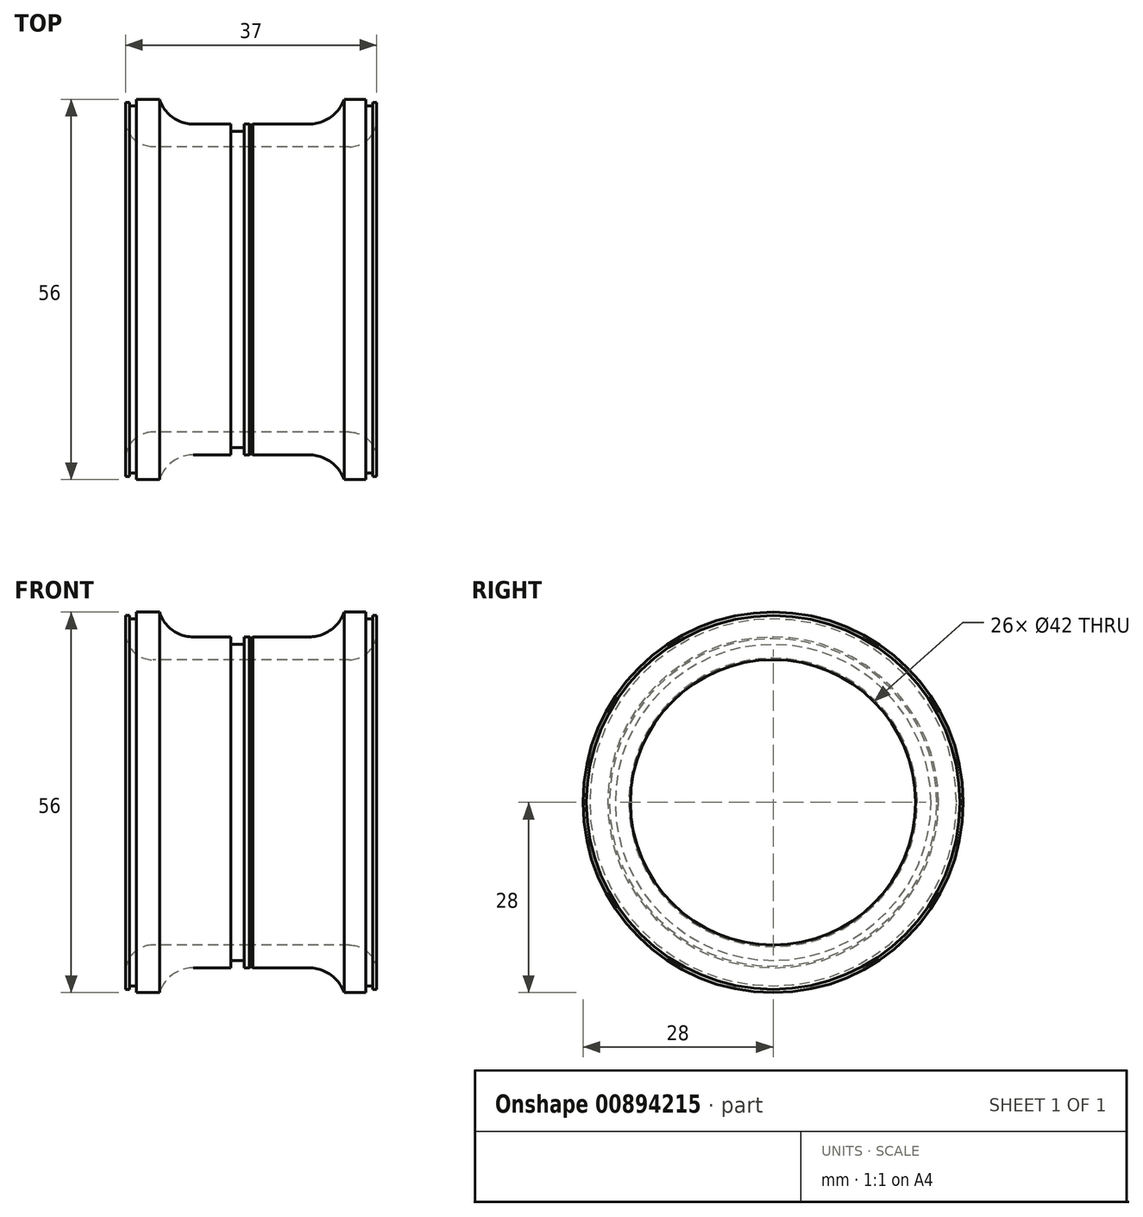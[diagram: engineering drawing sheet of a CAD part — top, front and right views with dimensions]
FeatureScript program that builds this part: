
annotation { "Feature Type Name" : "Feature", "Feature Type Description" : "" }
export const myFeature = defineFeature(function(context is Context, id is Id, definition is map)
    precondition{}
    {
        {
            var Q0;
            Q0=qCreatedBy(makeId("Front.planeOp"),FACE);
            var sketch = newSketch(context, id + "F0", { "sketchPlane" : qUnion([Q0])});
            skLineSegment(sketch, "E0", {"start": v(18.25, 21) * mm, "end": v(18.5, 21.25) * mm});
            skLineSegment(sketch, "E1", {"start": v(4, 21) * mm, "end": v(18.25, 21) * mm});
            skLineSegment(sketch, "E2", {"start": v(18.25, 24.35) * mm, "end": v(17.5, 24.35) * mm});
            skLineSegment(sketch, "E3", {"start": v(15.5, 24.35) * mm, "end": v(10, 24.35) * mm});
            skArc(sketch, "E4", {"start": v(5, 28) * mm, "mid": v(6.9, 25.36) * mm, "end": v(10, 24.35) * mm});
            skLineSegment(sketch, "E5", {"start": v(1.6, 28) * mm, "end": v(5, 28) * mm});
            skLineSegment(sketch, "E6", {"start": v(18.5, 24.1) * mm, "end": v(18.25, 24.35) * mm});
            skLineSegment(sketch, "E7", {"start": v(17.5, 23.25) * mm, "end": v(15.5, 23.25) * mm});
            skLineSegment(sketch, "E8", {"start": v(15.5, 23.25) * mm, "end": v(15.5, 24.35) * mm});
            skLineSegment(sketch, "E9", {"start": v(17.5, 24.35) * mm, "end": v(17.5, 23.25) * mm});
            skArc(sketch, "E10", {"start": v(0, 25) * mm, "mid": v(1.17, 22.17) * mm, "end": v(4, 21) * mm});
            skLineSegment(sketch, "E11", {"start": v(0, 27.5) * mm, "end": v(0.6, 27.5) * mm});
            skLineSegment(sketch, "E12", {"start": v(0.6, 27.5) * mm, "end": v(0.6, 27) * mm});
            skLineSegment(sketch, "E13", {"start": v(0.6, 27) * mm, "end": v(1.6, 27) * mm});
            skLineSegment(sketch, "E14", {"start": v(1.6, 27) * mm, "end": v(1.6, 28) * mm});
            skLineSegment(sketch, "E15", {"start": v(18.75, 21) * mm, "end": v(18.5, 21.25) * mm});
            skLineSegment(sketch, "E16", {"start": v(33, 21) * mm, "end": v(18.75, 21) * mm});
            skLineSegment(sketch, "E17", {"start": v(18.75, 24.35) * mm, "end": v(27, 24.35) * mm});
            skArc(sketch, "E18", {"start": v(27, 24.35) * mm, "mid": v(30.18, 25.35) * mm, "end": v(32.21, 28) * mm});
            skLineSegment(sketch, "E19", {"start": v(35.4, 28) * mm, "end": v(32.21, 28) * mm});
            skLineSegment(sketch, "E20", {"start": v(18.5, 24.1) * mm, "end": v(18.75, 24.35) * mm});
            skArc(sketch, "E21", {"start": v(33, 21) * mm, "mid": v(35.83, 22.17) * mm, "end": v(37, 25) * mm});
            skLineSegment(sketch, "E22", {"start": v(37, 27.5) * mm, "end": v(36.4, 27.5) * mm});
            skLineSegment(sketch, "E23", {"start": v(36.4, 27.5) * mm, "end": v(36.4, 27) * mm});
            skLineSegment(sketch, "E24", {"start": v(36.4, 27) * mm, "end": v(35.4, 27) * mm});
            skLineSegment(sketch, "E25", {"start": v(35.4, 27) * mm, "end": v(35.4, 28) * mm});
            skLineSegment(sketch, "E26", {"start": v(0, 27.5) * mm, "end": v(0, 25) * mm});
            skLineSegment(sketch, "E27", {"start": v(37, 27.5) * mm, "end": v(37, 25) * mm});
            skLineSegment(sketch, "E28", {"start": v(0, 0) * mm, "end": v(37, 0) * mm});
            skSolve(sketch);
        }
        {
            var Q0;
            Q0=makeQuery(id+"F0.imprint","IMPRINT",FACE,{"disambiguationData":[TD([[makeQuery(id+"F0.imprint","IMPRINT",EDGE,{"derivedFrom":sQuery(id+"F0.wireOp",EDGE,"E0")}),1.0]])]});
            var Q1;
            Q1=sQuery(id+"F0.wireOp",EDGE,"E28");
            revolve(context, id + "F1", {"surfaceOperationType" : NewSurfaceOperationType.NEW, "entities" : qUnion([Q0]), "axis" : qUnion([Q1]), "revolveType" : RevolveType.FULL});
        }
    });
